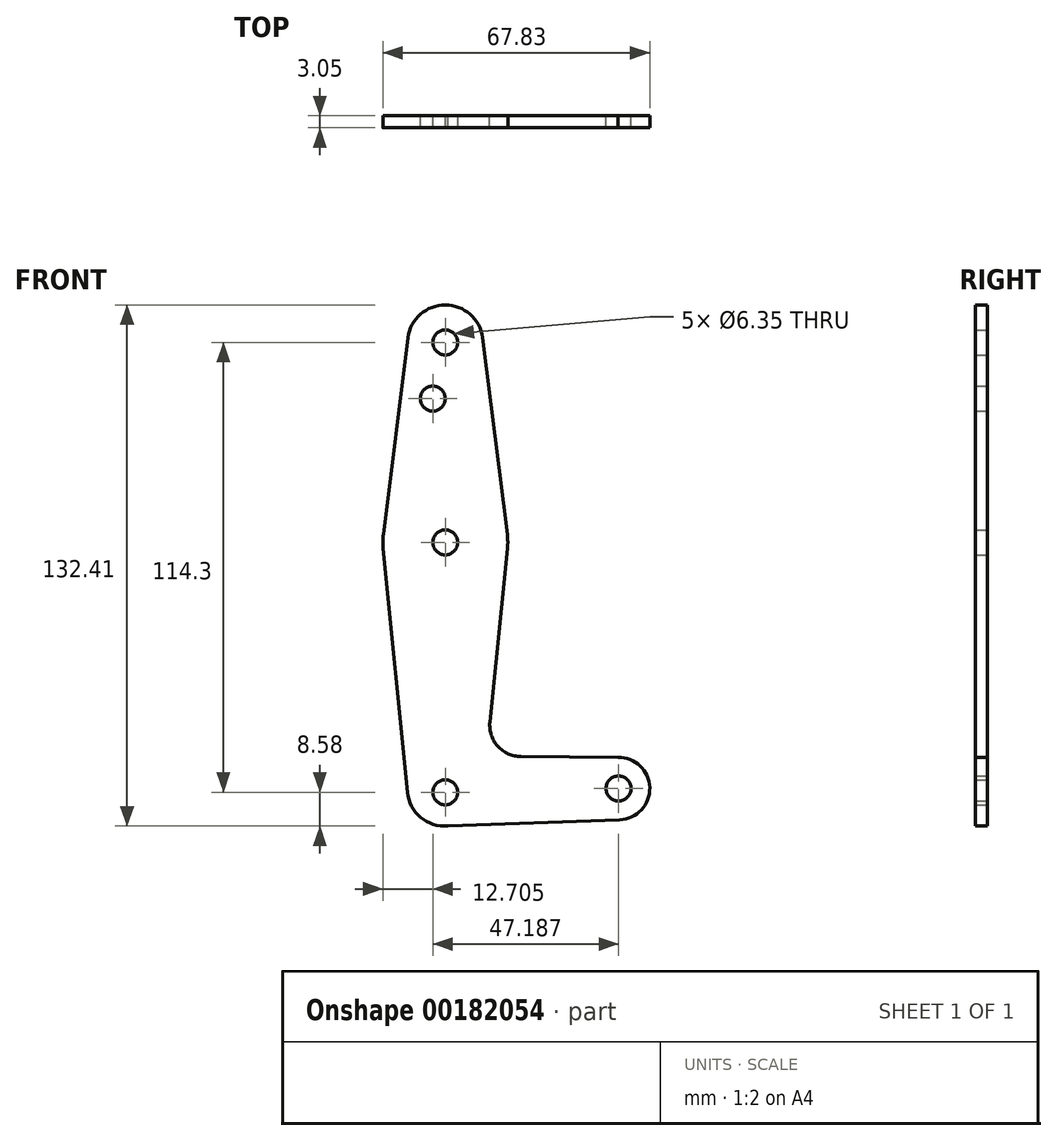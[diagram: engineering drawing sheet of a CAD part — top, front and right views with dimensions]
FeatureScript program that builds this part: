
annotation { "Feature Type Name" : "Feature", "Feature Type Description" : "" }
export const myFeature = defineFeature(function(context is Context, id is Id, definition is map)
    precondition{}
    {
        {
            var Q0;
            Q0=qCreatedBy(makeId("Front.planeOp"),FACE);
            var sketch = newSketch(context, id + "F0", { "sketchPlane" : qUnion([Q0])});
            skLineSegment(sketch, "E0", {"start": v(0, 114.3) * mm, "end": v(0, 0) * mm});
            skCircle(sketch, "E1", {"center": v(0, 114.3) * mm, "radius": 9.53 * mm});
            skCircle(sketch, "E2", {"center": v(0, 63.5) * mm, "radius": 15.88 * mm});
            skCircle(sketch, "E3", {"center": v(44.01, 0.95) * mm, "radius": 7.94 * mm});
            skLineSegment(sketch, "E4", {"start": v(9.45, 115.5) * mm, "end": v(15.75, 65.48) * mm});
            skLineSegment(sketch, "E5", {"start": v(-15.8, 61.93) * mm, "end": v(-9.62, 0) * mm});
            skLineSegment(sketch, "E6", {"start": v(15.8, 61.9) * mm, "end": v(11.33, 17.83) * mm});
            skLineSegment(sketch, "E7", {"start": v(0, -8.57) * mm, "end": v(44.3, -6.98) * mm});
            skLineSegment(sketch, "E8", {"start": v(-9.45, 115.5) * mm, "end": v(-15.75, 65.48) * mm});
            skCircle(sketch, "E9", {"center": v(0, 114.3) * mm, "radius": 3.18 * mm});
            skCircle(sketch, "E10", {"center": v(0, 63.5) * mm, "radius": 3.18 * mm});
            skCircle(sketch, "E11", {"center": v(0, 0) * mm, "radius": 3.18 * mm});
            skCircle(sketch, "E12", {"center": v(44.01, 0.95) * mm, "radius": 3.18 * mm});
            skCircle(sketch, "E13", {"center": v(-3.18, 100.03) * mm, "radius": 3.18 * mm});
            skLineSegment(sketch, "E14.trimOffspring", {"start": v(19.18, 9.08) * mm, "end": v(44.3, 8.88) * mm});
            skPoint(sketch, "E15.visualSharp", {"position": v(10.45, 9.15) * mm});
            skArc(sketch, "E15.filletArc", {"start": v(11.33, 17.83) * mm, "mid": v(13.32, 11.72) * mm, "end": v(19.18, 9.08) * mm});
            skPoint(sketch, "E16.orphan", {"position": v(-9.62, 0) * mm});
            skArc(sketch, "E17.trimOffspring", {"start": v(-9.62, 0) * mm, "mid": v(-6.24, -6.37) * mm, "end": v(0.64, -8.55) * mm});
            skLineSegment(sketch, "E18.trimOffspring", {"start": v(36.07, 0.95) * mm, "end": v(44.01, 0.95) * mm});
            skSolve(sketch);
        }
        {
            var Q0;
            Q0 = qSketchRegion(id + "F0", true);
            extrude(context, id + "F1", {"entities" : qUnion([Q0]), "depth" : 3.05 * mm});
        }
    });
